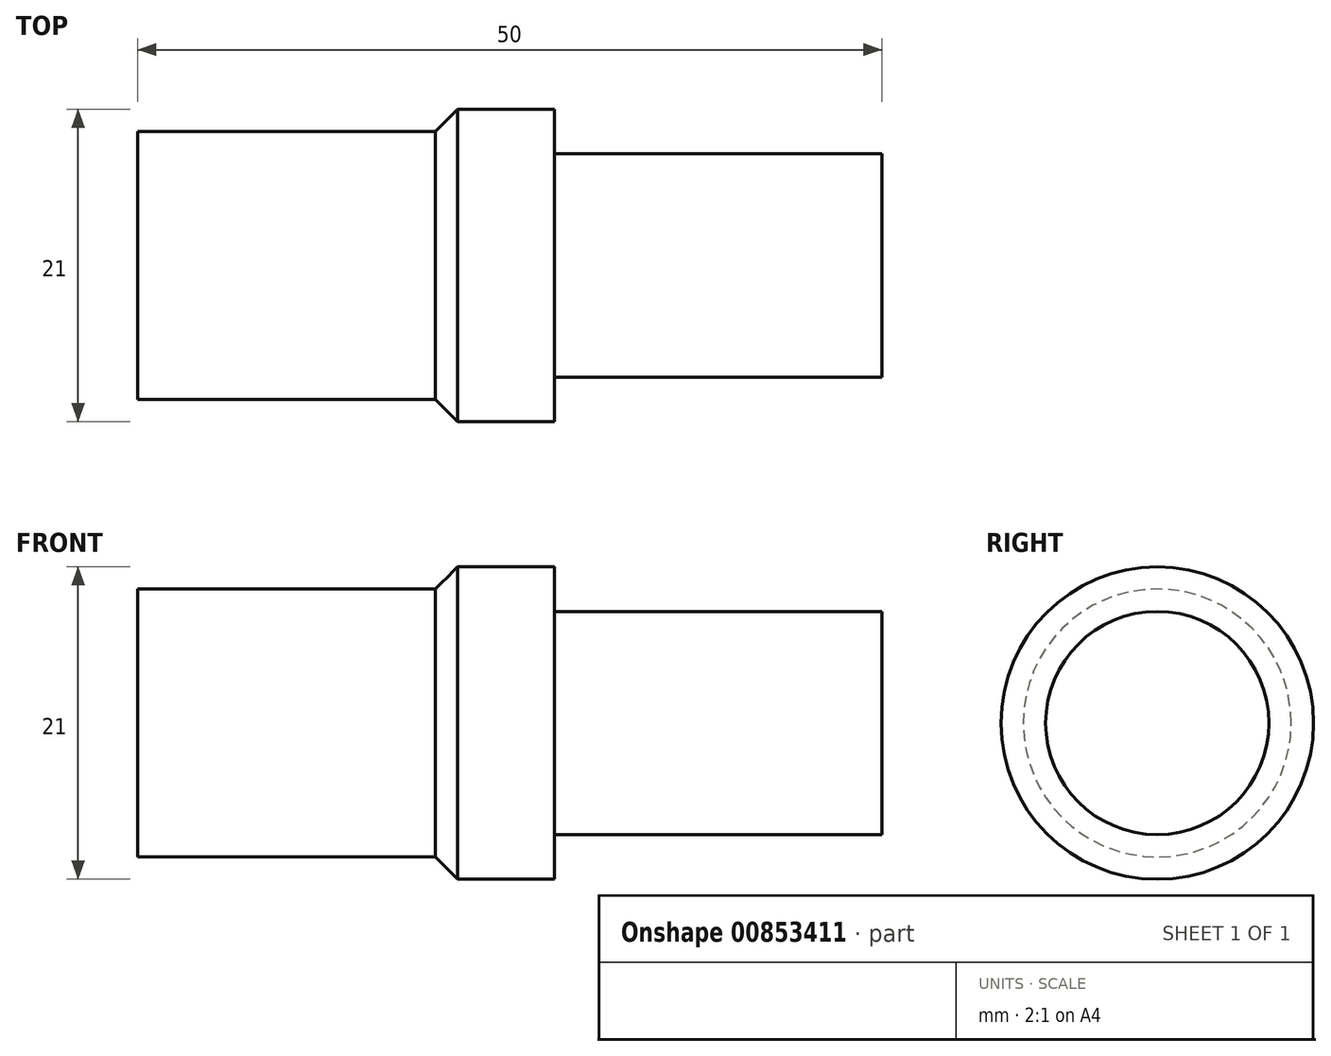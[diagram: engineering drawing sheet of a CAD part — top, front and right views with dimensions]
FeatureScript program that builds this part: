
annotation { "Feature Type Name" : "Feature", "Feature Type Description" : "" }
export const myFeature = defineFeature(function(context is Context, id is Id, definition is map)
    precondition{}
    {
        {
            var Q0;
            Q0=qCreatedBy(makeId("Front.planeOp"),FACE);
            var sketch = newSketch(context, id + "F0", { "sketchPlane" : qUnion([Q0])});
            skLineSegment(sketch, "E0", {"start": v(-50, 0) * mm, "end": v(0, 0) * mm, "construction": true});
            skLineSegment(sketch, "E1", {"start": v(-50, 0) * mm, "end": v(-50, 9) * mm, "construction": true});
            skLineSegment(sketch, "E2", {"start": v(-50, 9) * mm, "end": v(-30, 9) * mm, "construction": true});
            skLineSegment(sketch, "E3", {"start": v(-30, 9) * mm, "end": v(-28.5, 10.5) * mm, "construction": true});
            skLineSegment(sketch, "E4", {"start": v(-28.5, 10.5) * mm, "end": v(-22, 10.5) * mm, "construction": true});
            skLineSegment(sketch, "E5", {"start": v(-22, 10.5) * mm, "end": v(-22, 7.5) * mm, "construction": true});
            skLineSegment(sketch, "E6", {"start": v(-22, 7.5) * mm, "end": v(0, 7.5) * mm, "construction": true});
            skLineSegment(sketch, "E7", {"start": v(0, 7.5) * mm, "end": v(0, 0) * mm, "construction": true});
            skSolve(sketch);
        }
        {
            var Q0;
            Q0=qCreatedBy(makeId("Front.planeOp"),FACE);
            var sketch = newSketch(context, id + "F1", { "sketchPlane" : qUnion([Q0])});
            skLineSegment(sketch, "E8.0", {"start": v(-28.5, 10.5) * mm, "end": v(-22, 10.5) * mm});
            skLineSegment(sketch, "E8.1", {"start": v(-50, 0) * mm, "end": v(0, 0) * mm});
            skLineSegment(sketch, "E8.2", {"start": v(-22, 7.5) * mm, "end": v(0, 7.5) * mm});
            skLineSegment(sketch, "E8.3", {"start": v(0, 7.5) * mm, "end": v(0, 0) * mm});
            skLineSegment(sketch, "E8.4", {"start": v(-50, 9) * mm, "end": v(-30, 9) * mm});
            skLineSegment(sketch, "E8.5", {"start": v(-50, 0) * mm, "end": v(-50, 9) * mm});
            skLineSegment(sketch, "E9.0", {"start": v(-22, 10.5) * mm, "end": v(-22, 7.5) * mm});
            skLineSegment(sketch, "E10.0", {"start": v(-30, 9) * mm, "end": v(-28.5, 10.5) * mm});
            skSolve(sketch);
        }
        {
            var Q0;
            Q0=makeQuery(id+"F1.imprint","IMPRINT",FACE,{"disambiguationData":[TD([[makeQuery(id+"F1.imprint","IMPRINT",EDGE,{"derivedFrom":sQuery(id+"F1.wireOp",EDGE,"E8.0")}),-1.0]])]});
            var Q1;
            Q1=sQuery(id+"F1.wireOp",EDGE,"E8.1");
            revolve(context, id + "F2", {"surfaceOperationType" : NewSurfaceOperationType.NEW, "entities" : qUnion([Q0]), "axis" : qUnion([Q1]), "revolveType" : RevolveType.FULL});
        }
    });
